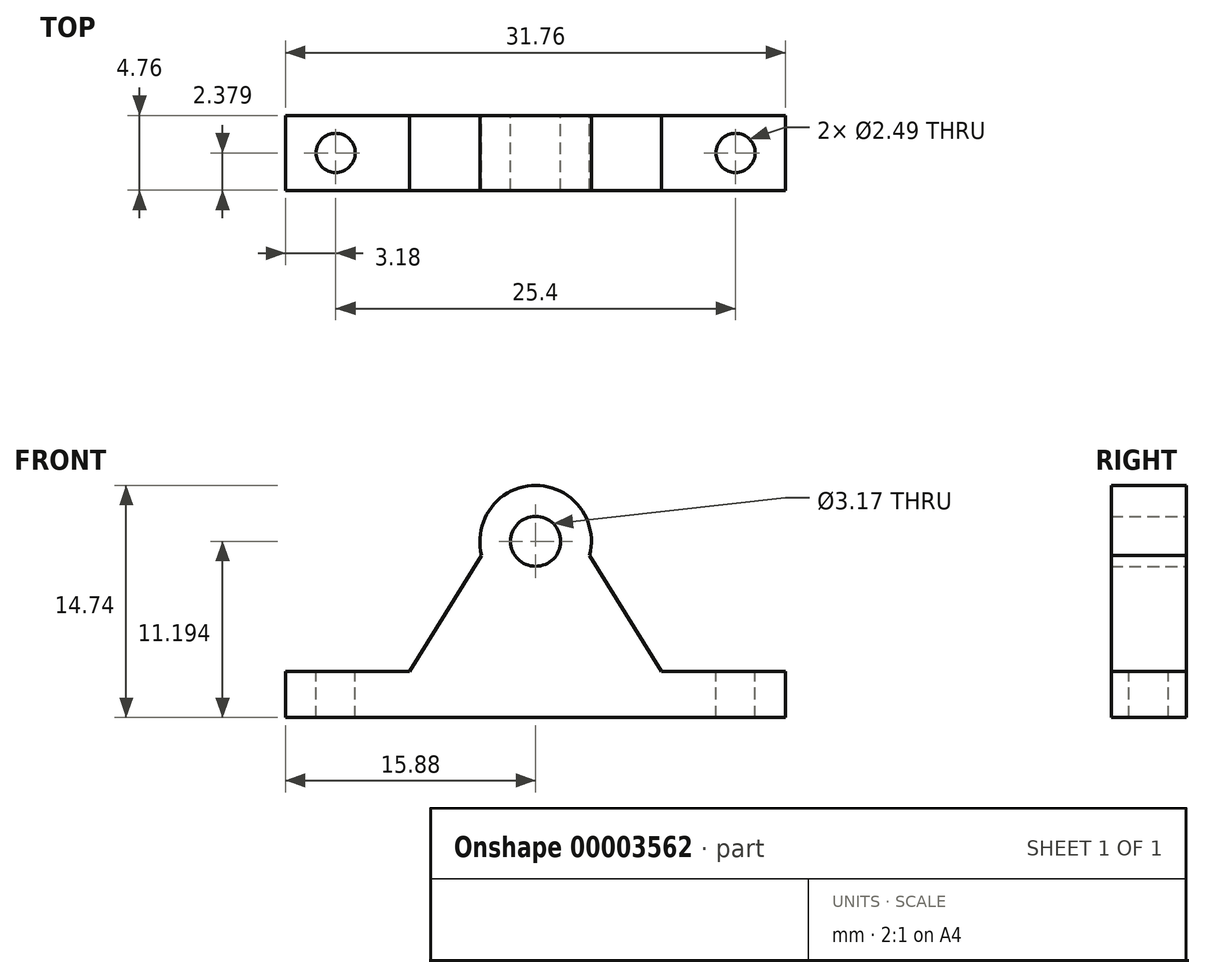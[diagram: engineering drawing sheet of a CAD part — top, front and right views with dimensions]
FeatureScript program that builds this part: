
annotation { "Feature Type Name" : "Feature", "Feature Type Description" : "" }
export const myFeature = defineFeature(function(context is Context, id is Id, definition is map)
    precondition{}
    {
        {
            var Q0;
            Q0=qCreatedBy(makeId("Front.planeOp"),FACE);
            var sketch = newSketch(context, id + "F0", { "sketchPlane" : qUnion([Q0])});
            skLineSegment(sketch, "E0", {"start": v(-15.88, -0.64) * mm, "end": v(15.88, -0.64) * mm});
            skLineSegment(sketch, "E1", {"start": v(-15.88, -0.64) * mm, "end": v(-15.88, 0) * mm});
            skLineSegment(sketch, "E2", {"start": v(-15.88, 0) * mm, "end": v(-15.88, 2.29) * mm});
            skLineSegment(sketch, "E3", {"start": v(-15.88, 2.29) * mm, "end": v(-8, 2.29) * mm});
            skLineSegment(sketch, "E4", {"start": v(-8, 2.29) * mm, "end": v(-3.43, 9.66) * mm});
            skLineSegment(sketch, "E5", {"start": v(15.88, -0.64) * mm, "end": v(15.88, 0) * mm});
            skLineSegment(sketch, "E6", {"start": v(15.88, 0) * mm, "end": v(15.88, 2.29) * mm});
            skLineSegment(sketch, "E7", {"start": v(15.88, 2.29) * mm, "end": v(8, 2.29) * mm});
            skLineSegment(sketch, "E8", {"start": v(8, 2.29) * mm, "end": v(3.43, 9.66) * mm});
            skLineSegment(sketch, "E9", {"start": v(0, -0.63) * mm, "end": v(0, 14.1) * mm, "construction": true});
            skLineSegment(sketch, "E10", {"start": v(-3.43, 9.66) * mm, "end": v(3.43, 9.66) * mm, "construction": true});
            skPoint(sketch, "E11", {"position": v(0, 9.66) * mm});
            skArc(sketch, "E12", {"start": v(3.43, 9.66) * mm, "mid": v(0, 14.1) * mm, "end": v(-3.43, 9.66) * mm});
            skCircle(sketch, "E13", {"center": v(0, 10.55) * mm, "radius": 1.59 * mm});
            skSolve(sketch);
        }
        {
            var Q0;
            Q0 = qSketchRegion(id + "F0", true);
            extrude(context, id + "F1", {"entities" : qUnion([Q0]), "depth" : 4.76 * mm});
        }
        {
            var Q0;
            Q0=makeQuery(id+"F1.opExtrude","SWEPT_FACE",FACE,{"disambiguationData":[OSD([sQuery(id+"F0.wireOp",EDGE,"E3")])]});
            var sketch = newSketch(context, id + "F2", { "sketchPlane" : qUnion([Q0])});
            skLineSegment(sketch, "E14", {"start": v(-15.88, -2.38) * mm, "end": v(15.88, -2.38) * mm, "construction": true});
            skCircle(sketch, "E15", {"center": v(-12.7, -2.38) * mm, "radius": 1.24 * mm});
            skCircle(sketch, "E16", {"center": v(12.7, -2.38) * mm, "radius": 1.24 * mm});
            skSolve(sketch);
        }
        {
            var Q0;
            Q0 = qSketchRegion(id + "F2", true);
            extrude(context, id + "F3", {"entities" : qUnion([Q0]), "operationType" : NewBodyOperationType.REMOVE, "endBound" : BoundingType.UP_TO_NEXT, "oppositeDirection" : true, "depth" : 25.4 * mm});
        }
    });
